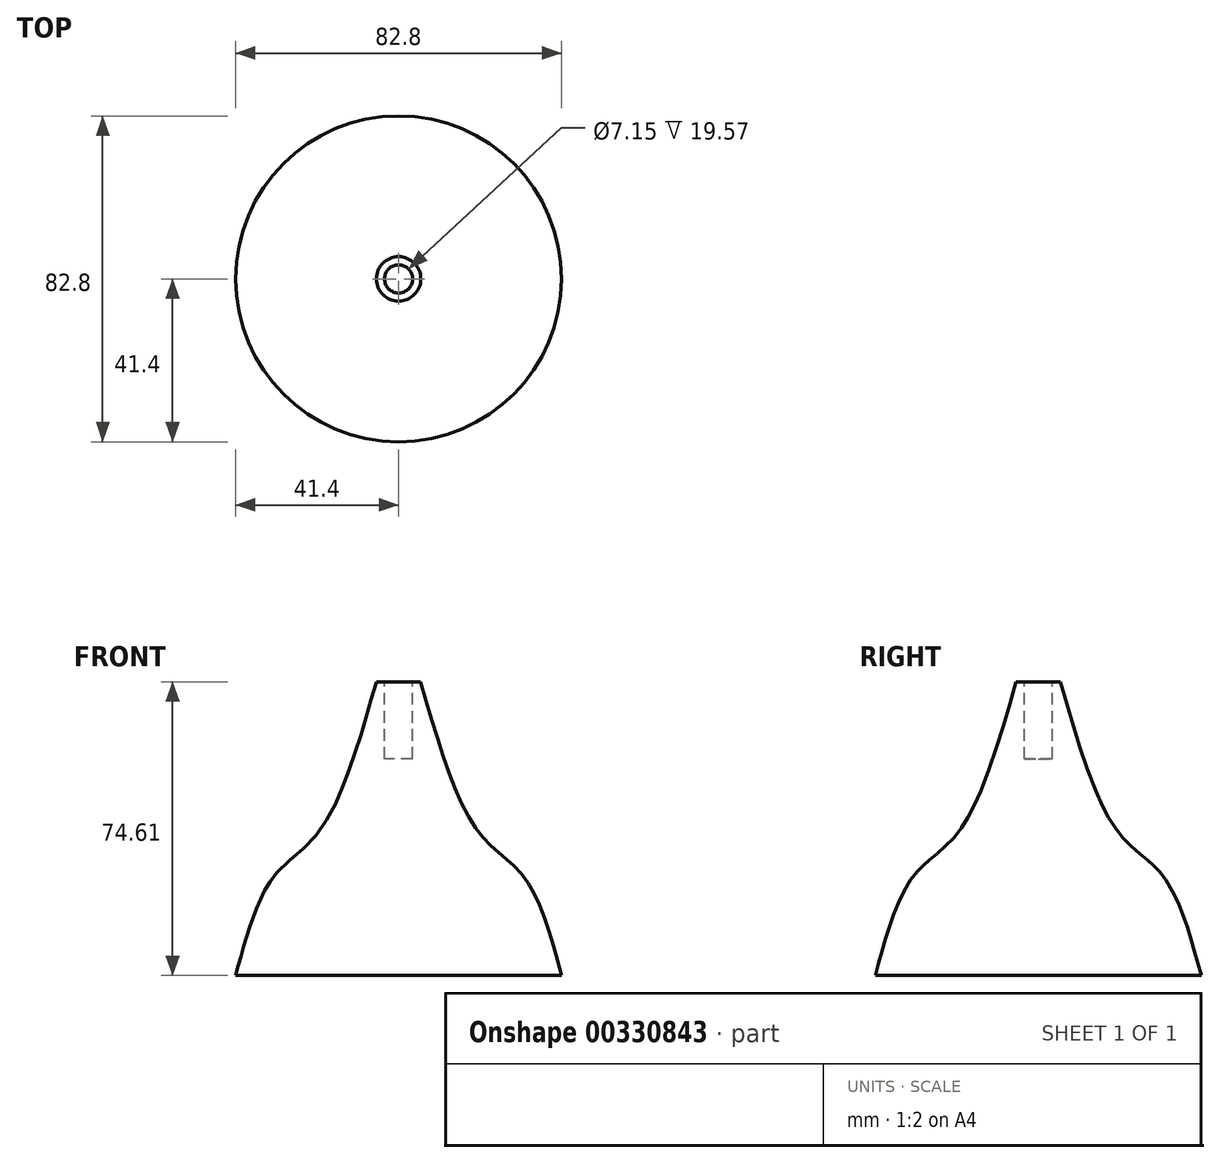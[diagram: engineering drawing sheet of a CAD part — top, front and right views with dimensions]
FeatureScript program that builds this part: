
annotation { "Feature Type Name" : "Feature", "Feature Type Description" : "" }
export const myFeature = defineFeature(function(context is Context, id is Id, definition is map)
    precondition{}
    {
        {
            var Q0;
            Q0=qCreatedBy(makeId("Front.planeOp"),FACE);
            var sketch = newSketch(context, id + "F0", { "sketchPlane" : qUnion([Q0])});
            skLineSegment(sketch, "E0", {"start": v(0, 0) * mm, "end": v(41.4, 0) * mm});
            skFitSpline(sketch, "E1", {"points": [v(41.4, 0) * mm, v(31.8, 25.12) * mm, v(20.32, 36.41) * mm, v(5.65, 74.61) * mm], "startDerivative": vector(-23.73, 87.66) * mm, "endDerivative": vector(-31.85, 111.14) * mm});
            skLineSegment(sketch, "E2", {"start": v(5.65, 74.61) * mm, "end": v(3.58, 74.61) * mm});
            skLineSegment(sketch, "E3", {"start": v(3.58, 74.61) * mm, "end": v(3.58, 55.04) * mm});
            skLineSegment(sketch, "E4", {"start": v(3.58, 55.04) * mm, "end": v(0, 55.04) * mm});
            skLineSegment(sketch, "E5", {"start": v(0, 55.04) * mm, "end": v(0, 0) * mm});
            skSolve(sketch);
        }
        {
            var Q0;
            Q0=makeQuery(id+"F0.imprint","IMPRINT",FACE,{"disambiguationData":[TD([[makeQuery(id+"F0.imprint","IMPRINT",EDGE,{"derivedFrom":sQuery(id+"F0.wireOp",EDGE,"E0")}),1.0]])]});
            var Q1;
            Q1=sQuery(id+"F0.wireOp",EDGE,"E5");
            revolve(context, id + "F1", {"entities" : qUnion([Q0]), "axis" : qUnion([Q1]), "revolveType" : RevolveType.FULL});
        }
    });
